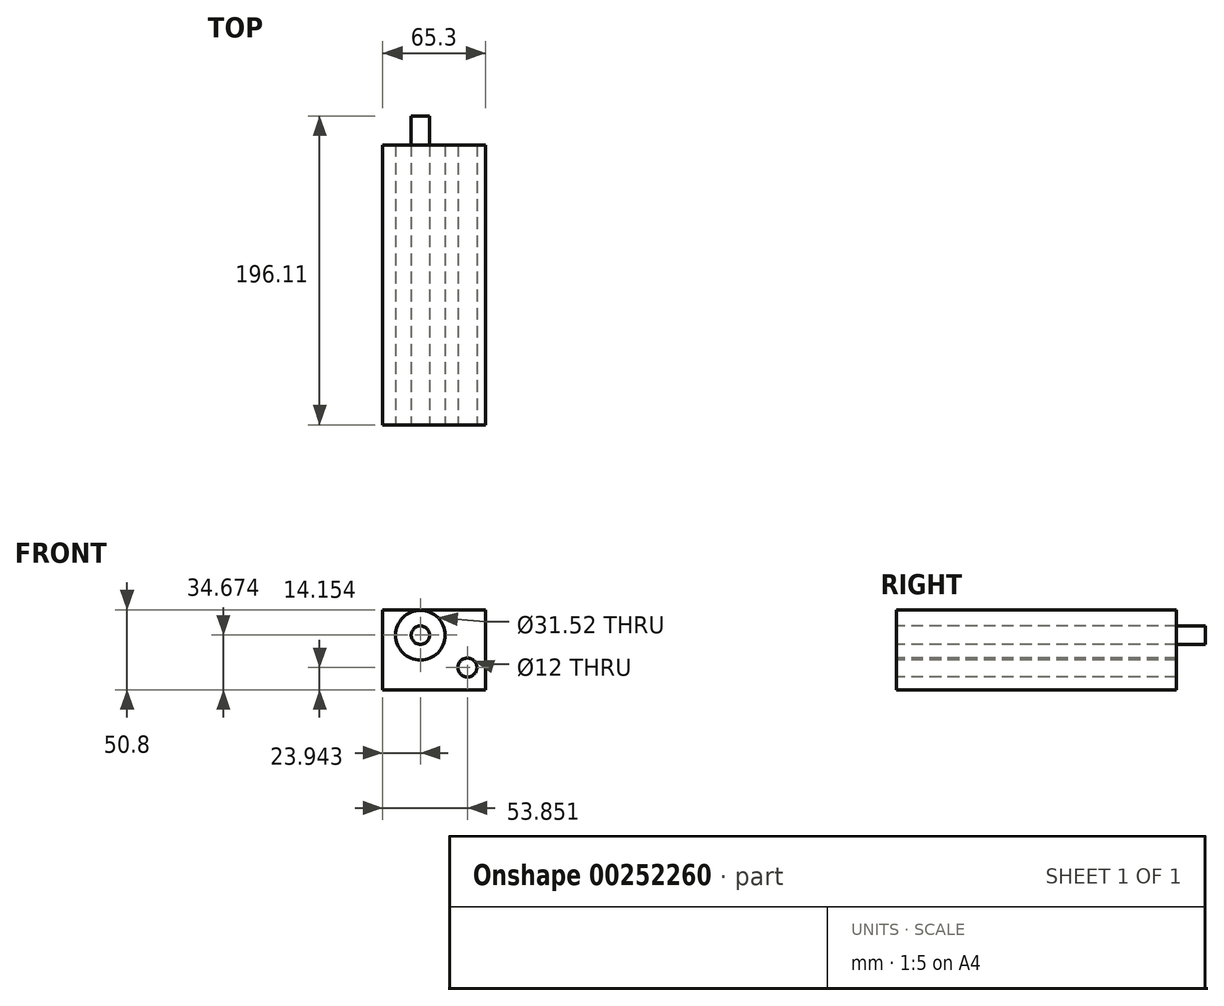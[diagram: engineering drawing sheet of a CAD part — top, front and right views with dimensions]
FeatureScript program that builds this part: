
annotation { "Feature Type Name" : "Feature", "Feature Type Description" : "" }
export const myFeature = defineFeature(function(context is Context, id is Id, definition is map)
    precondition{}
    {
        {
            var Q0;
            Q0=qCreatedBy(makeId("Front.planeOp"),FACE);
            var sketch = newSketch(context, id + "F0", { "sketchPlane" : qUnion([Q0])});
            skLineSegment(sketch, "E0.bottom", {"start": v(-10.15, 6.18) * mm, "end": v(10.15, 6.18) * mm});
            skLineSegment(sketch, "E0.top", {"start": v(-10.15, -6.18) * mm, "end": v(10.15, -6.18) * mm});
            skLineSegment(sketch, "E0.left", {"start": v(-10.15, 6.18) * mm, "end": v(-10.15, -6.18) * mm});
            skLineSegment(sketch, "E0.right", {"start": v(10.15, 6.18) * mm, "end": v(10.15, -6.18) * mm});
            skPoint(sketch, "E0.middle", {"position": v(0, 0) * mm});
            skLineSegment(sketch, "E1.bottom", {"start": v(-32.65, 25.4) * mm, "end": v(32.65, 25.4) * mm});
            skLineSegment(sketch, "E1.top", {"start": v(-32.65, -25.4) * mm, "end": v(32.65, -25.4) * mm});
            skLineSegment(sketch, "E1.left", {"start": v(-32.65, 25.4) * mm, "end": v(-32.65, -25.4) * mm});
            skLineSegment(sketch, "E1.right", {"start": v(32.65, 25.4) * mm, "end": v(32.65, -25.4) * mm});
            skSolve(sketch);
        }
        {
            var Q0;
            Q0 = qSketchRegion(id + "F0", true);
            var Q1;
            Q1=makeQuery(id+"F0.imprint","IMPRINT",FACE,{"disambiguationData":[TD([[makeQuery(id+"F0.imprint","IMPRINT",EDGE,{"derivedFrom":sQuery(id+"F0.wireOp",EDGE,"E0.bottom")}),-1.0]])]});
            extrude(context, id + "F1", {"entities" : qUnion([Q0, Q1]), "depth" : 177.8 * mm});
        }
        {
            var Q0;
            Q0=makeQuery(id+"F1.opExtrude","CAP_FACE",FACE,{"disambiguationData":[OSD([sQuery(id+"F0.wireOp",EDGE,"E1.bottom"),sQuery(id+"F0.wireOp",EDGE,"E1.top"),sQuery(id+"F0.wireOp",EDGE,"E1.left"),sQuery(id+"F0.wireOp",EDGE,"E1.right")])],"isStart":false});
            var sketch = newSketch(context, id + "F2", { "sketchPlane" : qUnion([Q0])});
            skCircle(sketch, "E2", {"center": v(-8.7, 9.27) * mm, "radius": 15.76 * mm});
            skCircle(sketch, "E3", {"center": v(-8.7, 9.27) * mm, "radius": 5.82 * mm});
            skCircle(sketch, "E4", {"center": v(21.2, -11.25) * mm, "radius": 6 * mm});
            skSolve(sketch);
        }
        {
            var Q0;
            Q0=makeQuery(id+"F2.imprint","IMPRINT",FACE,{"disambiguationData":[TD([[makeQuery(id+"F2.imprint","IMPRINT",EDGE,{"derivedFrom":sQuery(id+"F2.wireOp",EDGE,"E3")}),1.0]])]});
            extrude(context, id + "F3", {"entities" : qUnion([Q0]), "endBound" : BoundingType.THROUGH_ALL, "oppositeDirection" : true, "depth" : 25.4 * mm});
        }
        {
            var Q0;
            Q0 = qSketchRegion(id + "F2", true);
            extrude(context, id + "F4", {"entities" : qUnion([Q0]), "operationType" : NewBodyOperationType.REMOVE, "endBound" : BoundingType.THROUGH_ALL, "oppositeDirection" : true, "depth" : 25.4 * mm});
        }
    });
